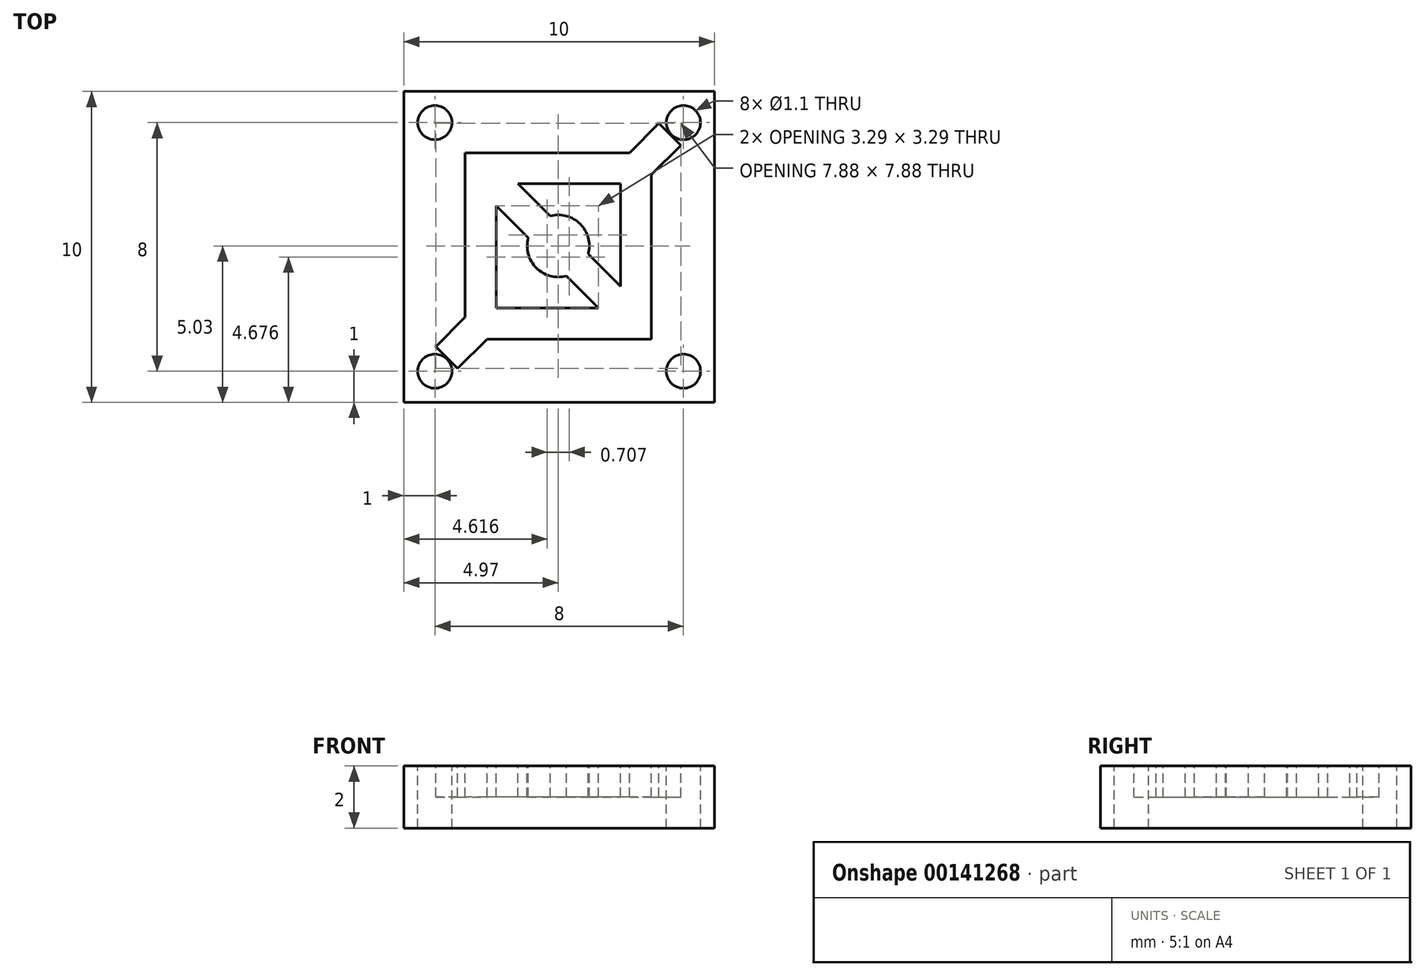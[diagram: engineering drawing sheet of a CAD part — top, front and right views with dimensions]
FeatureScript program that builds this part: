
annotation { "Feature Type Name" : "Feature", "Feature Type Description" : "" }
export const myFeature = defineFeature(function(context is Context, id is Id, definition is map)
    precondition{}
    {
        {
            var Q0;
            Q0=qCreatedBy(makeId("Top.planeOp"),FACE);
            var sketch = newSketch(context, id + "F0", { "sketchPlane" : qUnion([Q0])});
            skLineSegment(sketch, "E0.bottom", {"start": v(5.03, 4.97) * mm, "end": v(-4.97, 4.97) * mm});
            skLineSegment(sketch, "E0.top", {"start": v(5.03, -5.03) * mm, "end": v(-4.97, -5.03) * mm});
            skLineSegment(sketch, "E0.left", {"start": v(5.03, 4.97) * mm, "end": v(5.03, -5.03) * mm});
            skLineSegment(sketch, "E0.right", {"start": v(-4.97, 4.97) * mm, "end": v(-4.97, -5.03) * mm});
            skLineSegment(sketch, "E1.MirrorCS", {"start": v(-3.57, -3.6) * mm, "end": v(-3.94, -3.24) * mm});
            skLineSegment(sketch, "E2.MirrorCS", {"start": v(-3.57, -3.6) * mm, "end": v(-3.24, -3.94) * mm});
            skLineSegment(sketch, "E3.MirrorCS", {"start": v(3.6, 3.57) * mm, "end": v(3.24, 3.94) * mm});
            skLineSegment(sketch, "E4.MirrorCS", {"start": v(3.6, 3.57) * mm, "end": v(3.94, 3.24) * mm});
            skLineSegment(sketch, "E5", {"start": v(-3.94, -3.24) * mm, "end": v(-3, -2.3) * mm});
            skLineSegment(sketch, "E6", {"start": v(-3.24, -3.94) * mm, "end": v(-2.3, -3) * mm});
            skLineSegment(sketch, "E7.bottom", {"start": v(3, -3) * mm, "end": v(-2.3, -3) * mm});
            skLineSegment(sketch, "E7.top", {"start": v(2.3, 3) * mm, "end": v(-3, 3) * mm});
            skLineSegment(sketch, "E7.left", {"start": v(3, -3) * mm, "end": v(3, 2.3) * mm});
            skLineSegment(sketch, "E7.right", {"start": v(-3, -2.3) * mm, "end": v(-3, 3) * mm});
            skPoint(sketch, "E7.middle", {"position": v(0, 0) * mm});
            skLineSegment(sketch, "E8.bottom", {"start": v(1.3, -2) * mm, "end": v(-2, -2) * mm});
            skLineSegment(sketch, "E8.top", {"start": v(2, 2) * mm, "end": v(-1.3, 2) * mm});
            skLineSegment(sketch, "E8.left", {"start": v(2, -1.3) * mm, "end": v(2, 2) * mm});
            skLineSegment(sketch, "E8.right", {"start": v(-2, -2) * mm, "end": v(-2, 1.3) * mm});
            skLineSegment(sketch, "E9.trimOffspring", {"start": v(2.3, 3) * mm, "end": v(3.24, 3.94) * mm});
            skLineSegment(sketch, "E10.trimOffspring", {"start": v(3, 2.3) * mm, "end": v(3.94, 3.24) * mm});
            skArc(sketch, "E11", {"start": v(0.97, -0.26) * mm, "mid": v(0.7, 0.7) * mm, "end": v(-0.26, 0.97) * mm});
            skLineSegment(sketch, "E12", {"start": v(-0.97, 0.26) * mm, "end": v(-2, 1.3) * mm});
            skLineSegment(sketch, "E13", {"start": v(-0.26, 0.97) * mm, "end": v(-1.3, 2) * mm});
            skLineSegment(sketch, "E14", {"start": v(0.26, -0.97) * mm, "end": v(1.3, -2) * mm});
            skLineSegment(sketch, "E15", {"start": v(0.97, -0.26) * mm, "end": v(2, -1.3) * mm});
            skArc(sketch, "E16.trimOffspring", {"start": v(-0.97, 0.26) * mm, "mid": v(-0.7, -0.7) * mm, "end": v(0.26, -0.97) * mm});
            skCircle(sketch, "E17", {"center": v(-3.97, -4.03) * mm, "radius": 0.55 * mm});
            skLineSegment(sketch, "E18", {"start": v(5.03, -0.03) * mm, "end": v(-4.97, -0.03) * mm, "construction": true});
            skLineSegment(sketch, "E19", {"start": v(0.03, 4.97) * mm, "end": v(0.03, -5.03) * mm, "construction": true});
            skCircle(sketch, "E20.MirrorC", {"center": v(4.03, -4.03) * mm, "radius": 0.55 * mm});
            skCircle(sketch, "E21.MirrorC", {"center": v(-3.97, 3.97) * mm, "radius": 0.55 * mm});
            skCircle(sketch, "E22.MirrorC", {"center": v(4.03, 3.97) * mm, "radius": 0.55 * mm});
            skSolve(sketch);
        }
        {
            var Q0;
            Q0=makeQuery(id+"F0.imprint","IMPRINT",FACE,{"disambiguationData":[TD([[makeQuery(id+"F0.imprint","IMPRINT",EDGE,{"derivedFrom":sQuery(id+"F0.wireOp",EDGE,"E0.bottom")}),1.0]])]});
            var Q1;
            Q1=makeQuery(id+"F0.imprint","IMPRINT",FACE,{"disambiguationData":[TD([[makeQuery(id+"F0.imprint","IMPRINT",EDGE,{"derivedFrom":sQuery(id+"F0.wireOp",EDGE,"E1.MirrorCS")}),-1.0]])]});
            var Q2;
            Q2=makeQuery(id+"F0.imprint","IMPRINT",FACE,{"disambiguationData":[TD([[makeQuery(id+"F0.imprint","IMPRINT",EDGE,{"derivedFrom":sQuery(id+"F0.wireOp",EDGE,"E8.bottom")}),-1.0]])]});
            var Q3;
            Q3=makeQuery(id+"F0.imprint","IMPRINT",FACE,{"disambiguationData":[TD([[makeQuery(id+"F0.imprint","IMPRINT",EDGE,{"derivedFrom":sQuery(id+"F0.wireOp",EDGE,"E8.top")}),1.0]])]});
            extrude(context, id + "F1", {"entities" : qUnion([Q0, Q1, Q2, Q3]), "oppositeDirection" : true, "depth" : 2 * mm});
        }
        {
            var Q0;
            Q0=makeQuery(id+"F0.imprint","IMPRINT",FACE,{"disambiguationData":[TD([[makeQuery(id+"F0.imprint","IMPRINT",EDGE,{"derivedFrom":sQuery(id+"F0.wireOp",EDGE,"E1.MirrorCS")}),-1.0]])]});
            extrude(context, id + "F2", {"entities" : qUnion([Q0]), "operationType" : NewBodyOperationType.REMOVE, "oppositeDirection" : true, "depth" : 1 * mm});
        }
    });
